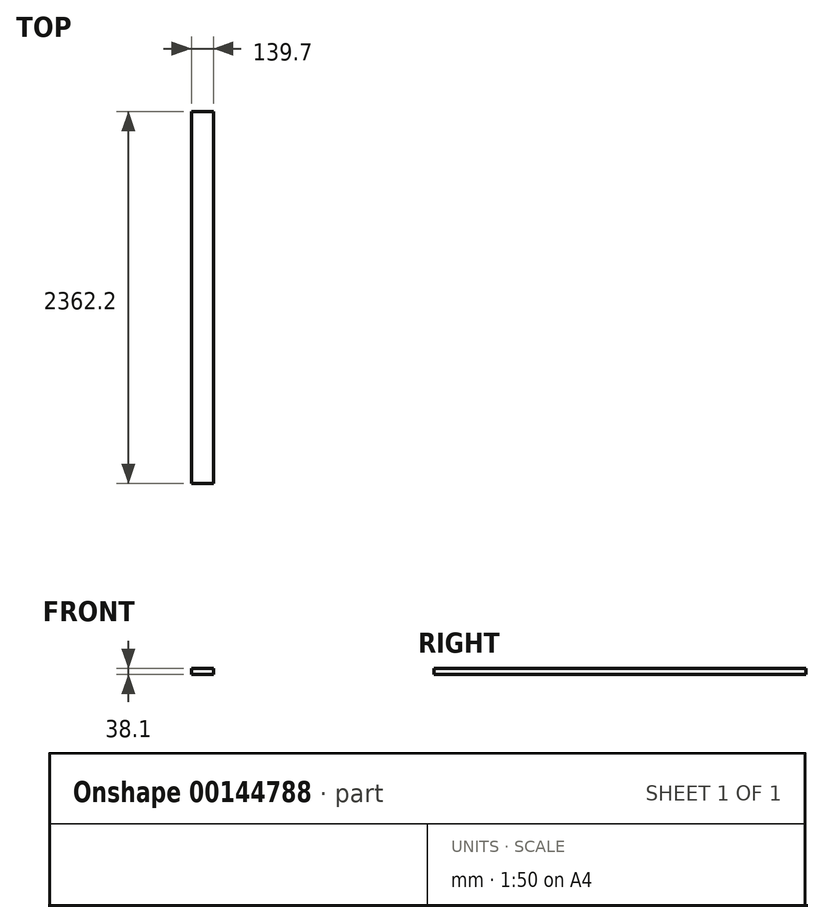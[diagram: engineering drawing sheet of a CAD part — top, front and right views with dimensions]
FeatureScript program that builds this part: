
annotation { "Feature Type Name" : "Feature", "Feature Type Description" : "" }
export const myFeature = defineFeature(function(context is Context, id is Id, definition is map)
    precondition{}
    {
        {
            var Q0;
            Q0=qCreatedBy(makeId("Front.planeOp"),FACE);
            var sketch = newSketch(context, id + "F0", { "sketchPlane" : qUnion([Q0])});
            skLineSegment(sketch, "E0.bottom", {"start": v(0, 0) * mm, "end": v(139.7, 0) * mm});
            skLineSegment(sketch, "E0.top", {"start": v(0, 38.1) * mm, "end": v(139.7, 38.1) * mm});
            skLineSegment(sketch, "E0.left", {"start": v(0, 0) * mm, "end": v(0, 38.1) * mm});
            skLineSegment(sketch, "E0.right", {"start": v(139.7, 0) * mm, "end": v(139.7, 38.1) * mm});
            skSolve(sketch);
        }
        {
            var Q0;
            Q0=makeQuery(id+"F0.imprint","IMPRINT",FACE,{"disambiguationData":[TD([[makeQuery(id+"F0.imprint","IMPRINT",EDGE,{"derivedFrom":sQuery(id+"F0.wireOp",EDGE,"E0.bottom")}),1.0]])]});
            extrude(context, id + "F1", {"entities" : qUnion([Q0]), "depth" : 2362.2 * mm});
        }
    });
